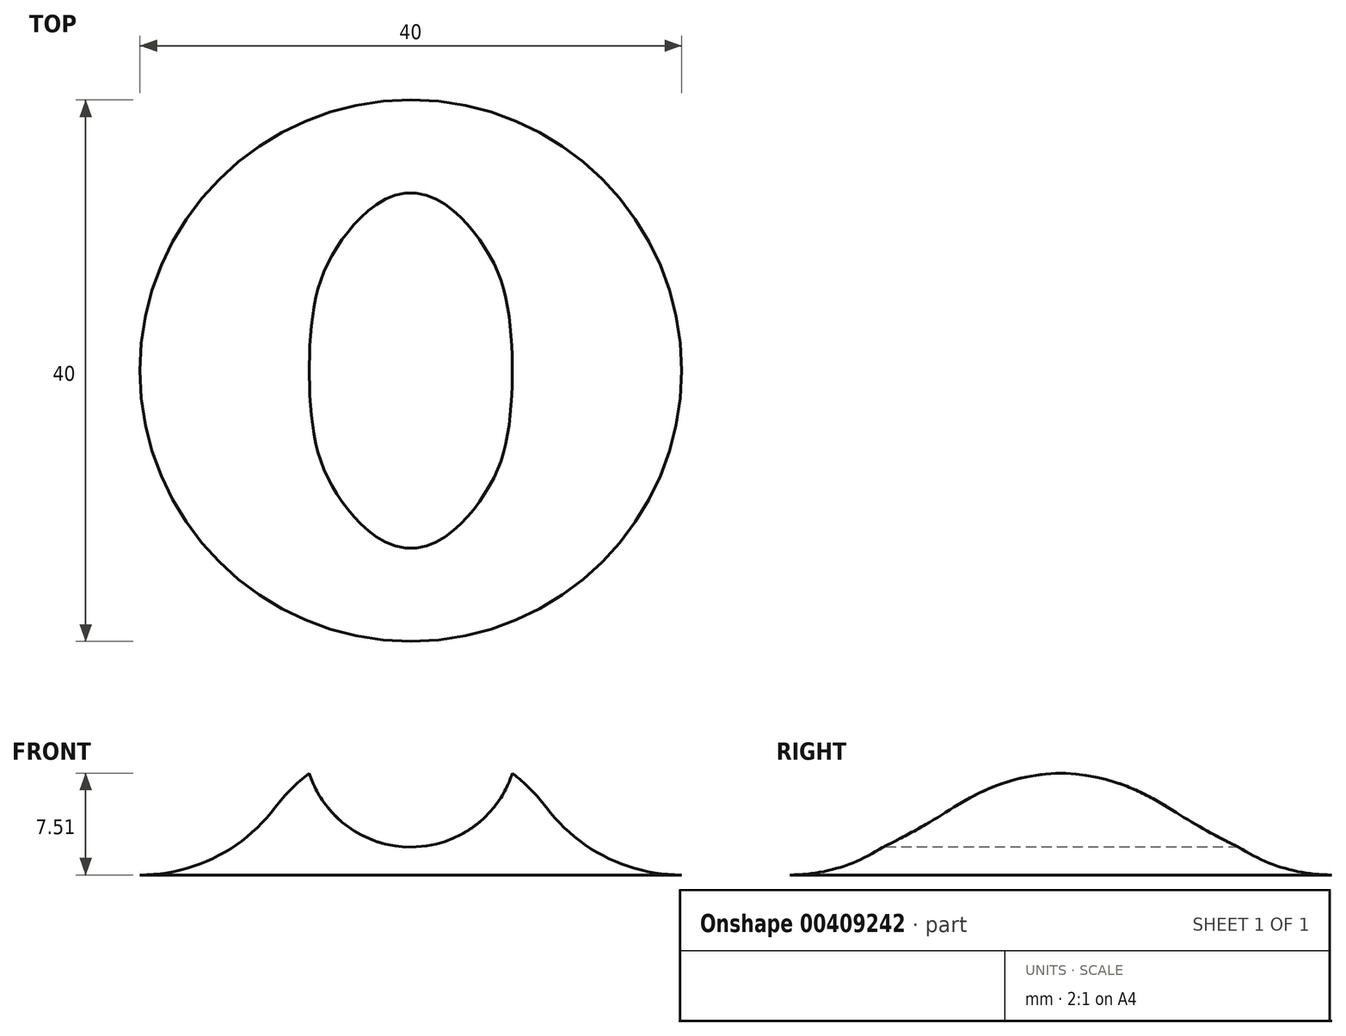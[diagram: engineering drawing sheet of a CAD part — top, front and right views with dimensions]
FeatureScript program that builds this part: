
annotation { "Feature Type Name" : "Feature", "Feature Type Description" : "" }
export const myFeature = defineFeature(function(context is Context, id is Id, definition is map)
    precondition{}
    {
        {
            var Q0;
            Q0=qCreatedBy(makeId("Front.planeOp"),FACE);
            var sketch = newSketch(context, id + "F0", { "sketchPlane" : qUnion([Q0])});
            skLineSegment(sketch, "E0", {"start": v(0, 0) * mm, "end": v(0, 10) * mm});
            skLineSegment(sketch, "E1", {"start": v(20, 0) * mm, "end": v(0, 0) * mm});
            skArc(sketch, "E2", {"start": v(10, 5) * mm, "mid": v(5.6, 8.68) * mm, "end": v(0, 10) * mm});
            skArc(sketch, "E3", {"start": v(10, 5) * mm, "mid": v(14.4, 1.32) * mm, "end": v(20, 0) * mm});
            skSolve(sketch);
        }
        {
            var Q0;
            Q0=makeQuery(id+"F0.imprint","IMPRINT",FACE,{"disambiguationData":[TD([[makeQuery(id+"F0.imprint","IMPRINT",EDGE,{"derivedFrom":sQuery(id+"F0.wireOp",EDGE,"E0")}),-1.0]])]});
            var Q1;
            Q1=sQuery(id+"F0.wireOp",EDGE,"E0");
            revolve(context, id + "F1", {"entities" : qUnion([Q0]), "axis" : qUnion([Q1]), "revolveType" : RevolveType.FULL});
        }
        {
            var Q0;
            Q0=qCreatedBy(makeId("Front.planeOp"),FACE);
            var sketch = newSketch(context, id + "F2", { "sketchPlane" : qUnion([Q0])});
            skCircle(sketch, "E4", {"center": v(0, 9.93) * mm, "radius": 7.88 * mm});
            skSolve(sketch);
        }
        {
            var Q0;
            Q0=makeQuery(id+"F2.imprint","IMPRINT",FACE,{"disambiguationData":[TD([[makeQuery(id+"F2.imprint","IMPRINT",EDGE,{"derivedFrom":sQuery(id+"F2.wireOp",EDGE,"E4")}),1.0]])]});
            extrude(context, id + "F3", {"entities" : qUnion([Q0]), "operationType" : NewBodyOperationType.REMOVE, "endBound" : BoundingType.SYMMETRIC, "oppositeDirection" : true, "depth" : 100 * mm});
        }
    });
